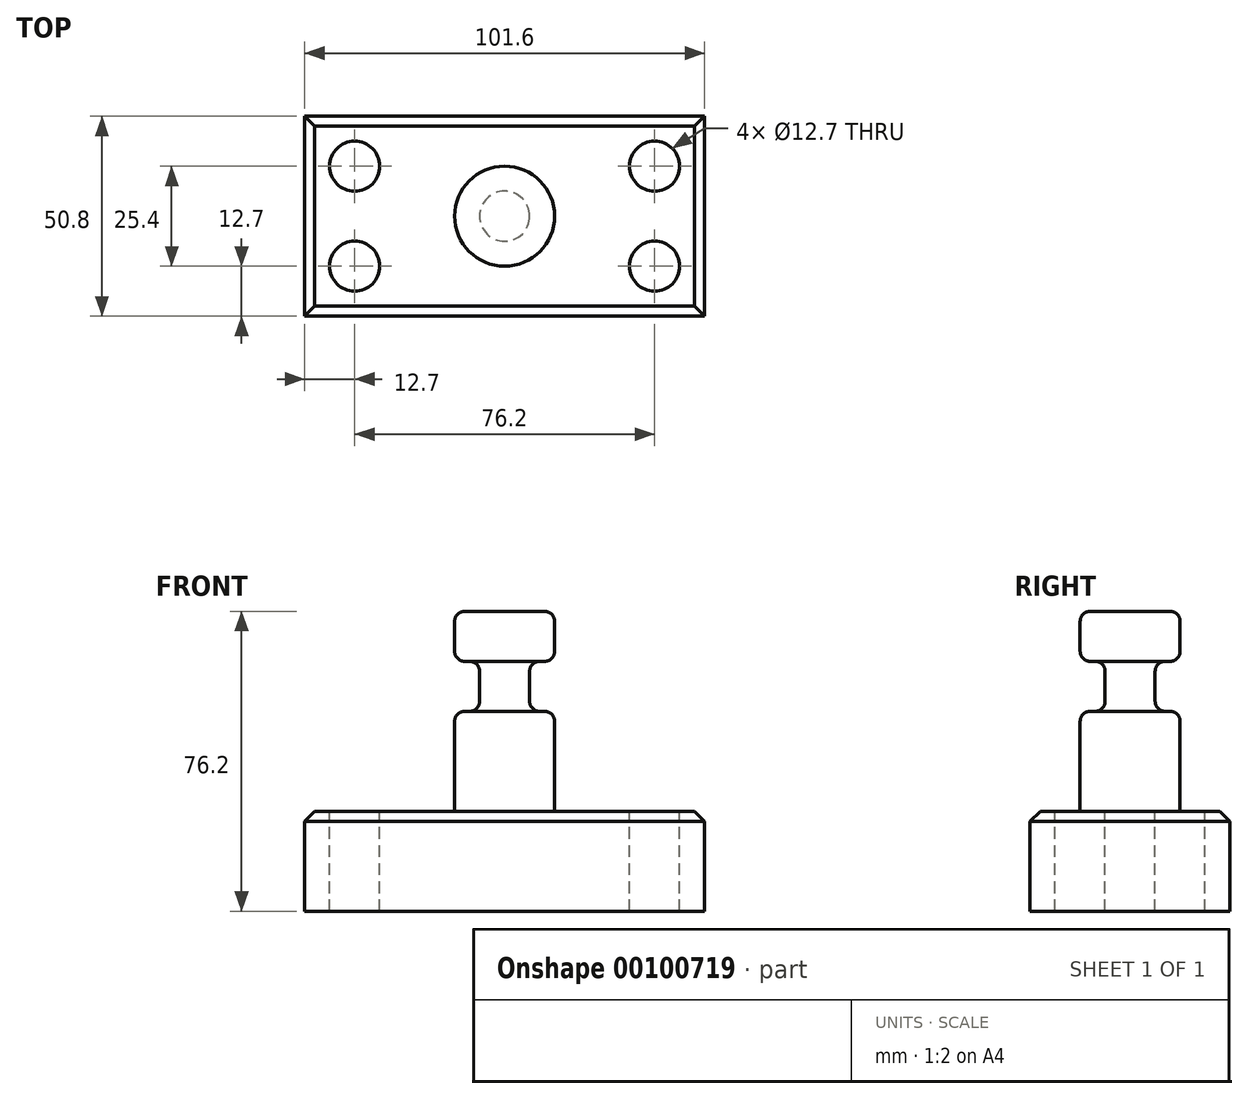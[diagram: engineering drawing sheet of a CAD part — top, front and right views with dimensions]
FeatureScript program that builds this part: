
annotation { "Feature Type Name" : "Feature", "Feature Type Description" : "" }
export const myFeature = defineFeature(function(context is Context, id is Id, definition is map)
    precondition{}
    {
        {
            var Q0;
            Q0=qCreatedBy(makeId("Top.planeOp"),FACE);
            var sketch = newSketch(context, id + "F0", { "sketchPlane" : qUnion([Q0])});
            skLineSegment(sketch, "E0.bottom", {"start": v(-50.8, 25.4) * mm, "end": v(50.8, 25.4) * mm});
            skLineSegment(sketch, "E0.top", {"start": v(-50.8, -25.4) * mm, "end": v(50.8, -25.4) * mm});
            skLineSegment(sketch, "E0.left", {"start": v(-50.8, 25.4) * mm, "end": v(-50.8, -25.4) * mm});
            skLineSegment(sketch, "E0.right", {"start": v(50.8, 25.4) * mm, "end": v(50.8, -25.4) * mm});
            skPoint(sketch, "E0.middle", {"position": v(0, 0) * mm});
            skSolve(sketch);
        }
        {
            var Q0;
            Q0=makeQuery(id+"F0.imprint","IMPRINT",FACE,{"disambiguationData":[TD([[makeQuery(id+"F0.imprint","IMPRINT",EDGE,{"derivedFrom":sQuery(id+"F0.wireOp",EDGE,"E0.bottom")}),-1.0]])]});
            extrude(context, id + "F1", {"entities" : qUnion([Q0]), "depth" : 25.4 * mm});
        }
        {
            var Q0;
            Q0=makeQuery(id+"F1.opExtrude","CAP_FACE",FACE,{"disambiguationData":[OSD([sQuery(id+"F0.wireOp",EDGE,"E0.bottom"),sQuery(id+"F0.wireOp",EDGE,"E0.top"),sQuery(id+"F0.wireOp",EDGE,"E0.left"),sQuery(id+"F0.wireOp",EDGE,"E0.right")])],"isStart":false});
            var sketch = newSketch(context, id + "F2", { "sketchPlane" : qUnion([Q0])});
            skCircle(sketch, "E1", {"center": v(-38.1, 12.7) * mm, "radius": 6.35 * mm});
            skCircle(sketch, "E2", {"center": v(38.1, 12.7) * mm, "radius": 6.35 * mm});
            skCircle(sketch, "E3", {"center": v(38.1, -12.7) * mm, "radius": 6.35 * mm});
            skCircle(sketch, "E4", {"center": v(-38.1, -12.7) * mm, "radius": 6.35 * mm});
            skSolve(sketch);
        }
        {
            var Q0;
            Q0=makeQuery(id+"F2.imprint","IMPRINT",FACE,{"disambiguationData":[TD([[makeQuery(id+"F2.imprint","IMPRINT",EDGE,{"derivedFrom":sQuery(id+"F2.wireOp",EDGE,"E1")}),1.0]])]});
            var Q1;
            Q1=makeQuery(id+"F2.imprint","IMPRINT",FACE,{"disambiguationData":[TD([[makeQuery(id+"F2.imprint","IMPRINT",EDGE,{"derivedFrom":sQuery(id+"F2.wireOp",EDGE,"E2")}),1.0]])]});
            var Q2;
            Q2=makeQuery(id+"F2.imprint","IMPRINT",FACE,{"disambiguationData":[TD([[makeQuery(id+"F2.imprint","IMPRINT",EDGE,{"derivedFrom":sQuery(id+"F2.wireOp",EDGE,"E4")}),1.0]])]});
            var Q3;
            Q3=makeQuery(id+"F2.imprint","IMPRINT",FACE,{"disambiguationData":[TD([[makeQuery(id+"F2.imprint","IMPRINT",EDGE,{"derivedFrom":sQuery(id+"F2.wireOp",EDGE,"E3")}),1.0]])]});
            extrude(context, id + "F3", {"entities" : qUnion([Q0, Q1, Q2, Q3]), "operationType" : NewBodyOperationType.REMOVE, "endBound" : BoundingType.THROUGH_ALL, "oppositeDirection" : true, "depth" : 25.4 * mm});
        }
        {
            var Q0;
            Q0=qCreatedBy(makeId("Front.planeOp"),FACE);
            var sketch = newSketch(context, id + "F4", { "sketchPlane" : qUnion([Q0])});
            skLineSegment(sketch, "E5.bottom", {"start": v(0, 25.4) * mm, "end": v(-12.7, 25.4) * mm});
            skLineSegment(sketch, "E5.top", {"start": v(0, 76.2) * mm, "end": v(-12.7, 76.2) * mm});
            skLineSegment(sketch, "E5.left", {"start": v(0, 25.4) * mm, "end": v(0, 76.2) * mm});
            skLineSegment(sketch, "E5.right", {"start": v(-12.7, 25.4) * mm, "end": v(-12.7, 76.2) * mm});
            skSolve(sketch);
        }
        {
            var Q0;
            Q0=makeQuery(id+"F4.imprint","IMPRINT",FACE,{"disambiguationData":[TD([[makeQuery(id+"F4.imprint","IMPRINT",EDGE,{"derivedFrom":sQuery(id+"F4.wireOp",EDGE,"E5.bottom")}),-1.0]])]});
            var Q1;
            Q1=sQuery(id+"F4.wireOp",EDGE,"E5.left");
            revolve(context, id + "F5", {"operationType" : NewBodyOperationType.ADD, "entities" : qUnion([Q0]), "axis" : qUnion([Q1]), "revolveType" : RevolveType.FULL});
        }
        {
            var Q0;
            Q0=qCreatedBy(makeId("Front.planeOp"),FACE);
            var sketch = newSketch(context, id + "F6", { "sketchPlane" : qUnion([Q0])});
            skLineSegment(sketch, "E6.bottom", {"start": v(-6.35, 63.5) * mm, "end": v(-17.85, 63.5) * mm});
            skLineSegment(sketch, "E6.top", {"start": v(-6.35, 50.8) * mm, "end": v(-17.85, 50.8) * mm});
            skLineSegment(sketch, "E6.left", {"start": v(-6.35, 63.5) * mm, "end": v(-6.35, 50.8) * mm});
            skLineSegment(sketch, "E6.right", {"start": v(-17.85, 63.5) * mm, "end": v(-17.85, 50.8) * mm});
            skLineSegment(sketch, "E7", {"start": v(0, 0) * mm, "end": v(0, 86.44) * mm, "construction": true});
            skSolve(sketch);
        }
        {
            var Q0;
            Q0=makeQuery(id+"F6.imprint","IMPRINT",FACE,{"disambiguationData":[TD([[makeQuery(id+"F6.imprint","IMPRINT",EDGE,{"derivedFrom":sQuery(id+"F6.wireOp",EDGE,"E6.bottom")}),1.0]])]});
            var Q1;
            Q1=sQuery(id+"F6.wireOp",EDGE,"E7");
            revolve(context, id + "F7", {"operationType" : NewBodyOperationType.REMOVE, "entities" : qUnion([Q0]), "axis" : qUnion([Q1]), "revolveType" : RevolveType.FULL, "oppositeDirection" : true});
        }
        {
            var Q0;
            Q0=makeQuery(id+"F7.boolean.opBoolean","INTERSECT",EDGE,{"derivedFrom":[makeQuery(id+"F5.opRevolve","SWEPT_FACE",FACE,{"disambiguationData":[OSD([sQuery(id+"F4.wireOp",EDGE,"E5.right")])]}),makeQuery(id+"F7.opRevolve","SWEPT_FACE",FACE,{"disambiguationData":[OSD([sQuery(id+"F6.wireOp",EDGE,"E6.top")])]})]});
            var Q1;
            Q1=makeQuery(id+"F5.opRevolve","SWEPT_EDGE",EDGE,{"disambiguationData":[OSD([sQuery(id+"F4.wireOp",EDGE,"E5.bottom"),sQuery(id+"F4.wireOp",EDGE,"E5.right")])]});
            var Q2;
            Q2=makeQuery(id+"F7.boolean.opBoolean","INTERSECT",EDGE,{"derivedFrom":[makeQuery(id+"F5.opRevolve","SWEPT_FACE",FACE,{"disambiguationData":[OSD([sQuery(id+"F4.wireOp",EDGE,"E5.right")])]}),makeQuery(id+"F7.opRevolve","SWEPT_FACE",FACE,{"disambiguationData":[OSD([sQuery(id+"F6.wireOp",EDGE,"E6.bottom")])]})]});
            var Q3;
            Q3=makeQuery(id+"F5.opRevolve","SWEPT_EDGE",EDGE,{"disambiguationData":[OSD([sQuery(id+"F4.wireOp",EDGE,"E5.top"),sQuery(id+"F4.wireOp",EDGE,"E5.right")])]});
            var Q4;
            Q4=makeQuery(id+"F7.boolean.opBoolean","COPY",EDGE,{"derivedFrom":makeQuery(id+"F7.opRevolve","SWEPT_EDGE",EDGE,{"disambiguationData":[OSD([sQuery(id+"F6.wireOp",EDGE,"E6.bottom"),sQuery(id+"F6.wireOp",EDGE,"E6.left")])]})});
            var Q5;
            Q5=makeQuery(id+"F7.boolean.opBoolean","COPY",EDGE,{"derivedFrom":makeQuery(id+"F7.opRevolve","SWEPT_EDGE",EDGE,{"disambiguationData":[OSD([sQuery(id+"F6.wireOp",EDGE,"E6.top"),sQuery(id+"F6.wireOp",EDGE,"E6.left")])]})});
            fillet(context, id + "F8", {"entities" : qUnion([Q0, Q1, Q2, Q3, Q4, Q5]), "radius" : 2.54 * mm, "tangentPropagation" : true, "allowEdgeOverflow" : false});
        }
        {
            var Q0;
            Q0=makeQuery(id+"F1.opExtrude","CAP_EDGE",EDGE,{"disambiguationData":[OSD([sQuery(id+"F0.wireOp",EDGE,"E0.top")])],"isStart":false});
            var Q1;
            Q1=makeQuery(id+"F1.opExtrude","CAP_EDGE",EDGE,{"disambiguationData":[OSD([sQuery(id+"F0.wireOp",EDGE,"E0.right")])],"isStart":false});
            var Q2;
            Q2=makeQuery(id+"F1.opExtrude","CAP_EDGE",EDGE,{"disambiguationData":[OSD([sQuery(id+"F0.wireOp",EDGE,"E0.bottom")])],"isStart":false});
            var Q3;
            Q3=makeQuery(id+"F1.opExtrude","CAP_EDGE",EDGE,{"disambiguationData":[OSD([sQuery(id+"F0.wireOp",EDGE,"E0.left")])],"isStart":false});
            chamfer(context, id + "F9", {"entities" : qUnion([Q0, Q1, Q2, Q3]), "width" : 2.54 * mm, "tangentPropagation" : true});
        }
    });
